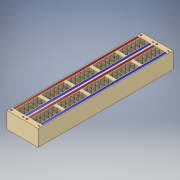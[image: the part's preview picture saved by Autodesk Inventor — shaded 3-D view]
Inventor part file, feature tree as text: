
AUTODESK INVENTOR PART (.ipt)
format: ipt  version: 2019 (Build 230136000, 136)  size: 966,144 bytes
history: native  units: in
note: dims shown in document units (in); Inventor stores cm internally (conversion verified against a paired STEP export)
features: extrude x4, sketch x4, plane x4, mirror x4, chamfer x1, pattern_linear x1
ambient origin geometry x8: Origin, YZ Plane, XZ Plane, XY Plane, X Axis, Y Axis, Z Axis, Center Point
bodies: Solid1 (feature_tree)
feature tree (18):
  extrude  "Extrusion1"  Depth=3.2382in
  sketch  "Sketch2"  dims[d2=0.3937in d3=0.0in d4=0.0984in d30=0.0098in d38=0.0098in]
  plane  "Work Plane1"
  plane  "Work Plane2"
  extrude  "Extrusion2"  Depth=0.0984in
  chamfer  "Chamfer1"  Distance=0.0098in
  pattern_linear  "Rectangular Pattern1"  Spacing1=0.1776in  [1 undecoded]
  mirror  "Mirror1"
  plane  "Work Plane3"
  plane  "Work Plane4"
  extrude  "Extrusion3"  Depth=0.1973in
  mirror  "Mirror2"
  mirror  "Mirror3"
  extrude  "Extrusion4"  Depth=0.2766in
  mirror  "Mirror4"
  sketch  "Sketch1"  dims[d0=0.75in d1=3.2382in]
  sketch  "Sketch3"  dims[d39=0.0098in]
  sketch  "Sketch4"  dims[d50=0.0984in d51=0.1776in d52=0.1973in d53=0.2766in d54=0.1353in d55=0.2269in d56=0.2466in d57=0.3282in d58=0.3479in d59=0.4296in d60=0.4493in d61=0.531in d62=0.5507in d63=0.6422in d64=0.0984in d65=0.0in d66=0.0098in d67=0.0492in d68=45.0deg d69=1.9685in d71=0.6152in d72=0.0221in d73=0.0453in d75=0.0886in d76=0.1255in d77=0.1255in d78=0.0in d79=0.0in d86=0.0453in d87=0.1255in d88=0.0401in d89=0.0302in d90=0.0151in d94=0.0151in d95=0.0453in d96=0.0151in d97=0.0302in d98=0.0151in d99=0.0151in d100=0.0151in d101=0.0in d102=0.0in]
note: 1 required parameter value undecoded (feature->parameter linkage not recoverable at this tier; creation-order binding heuristic only, values carry confidence <= 0.55)
